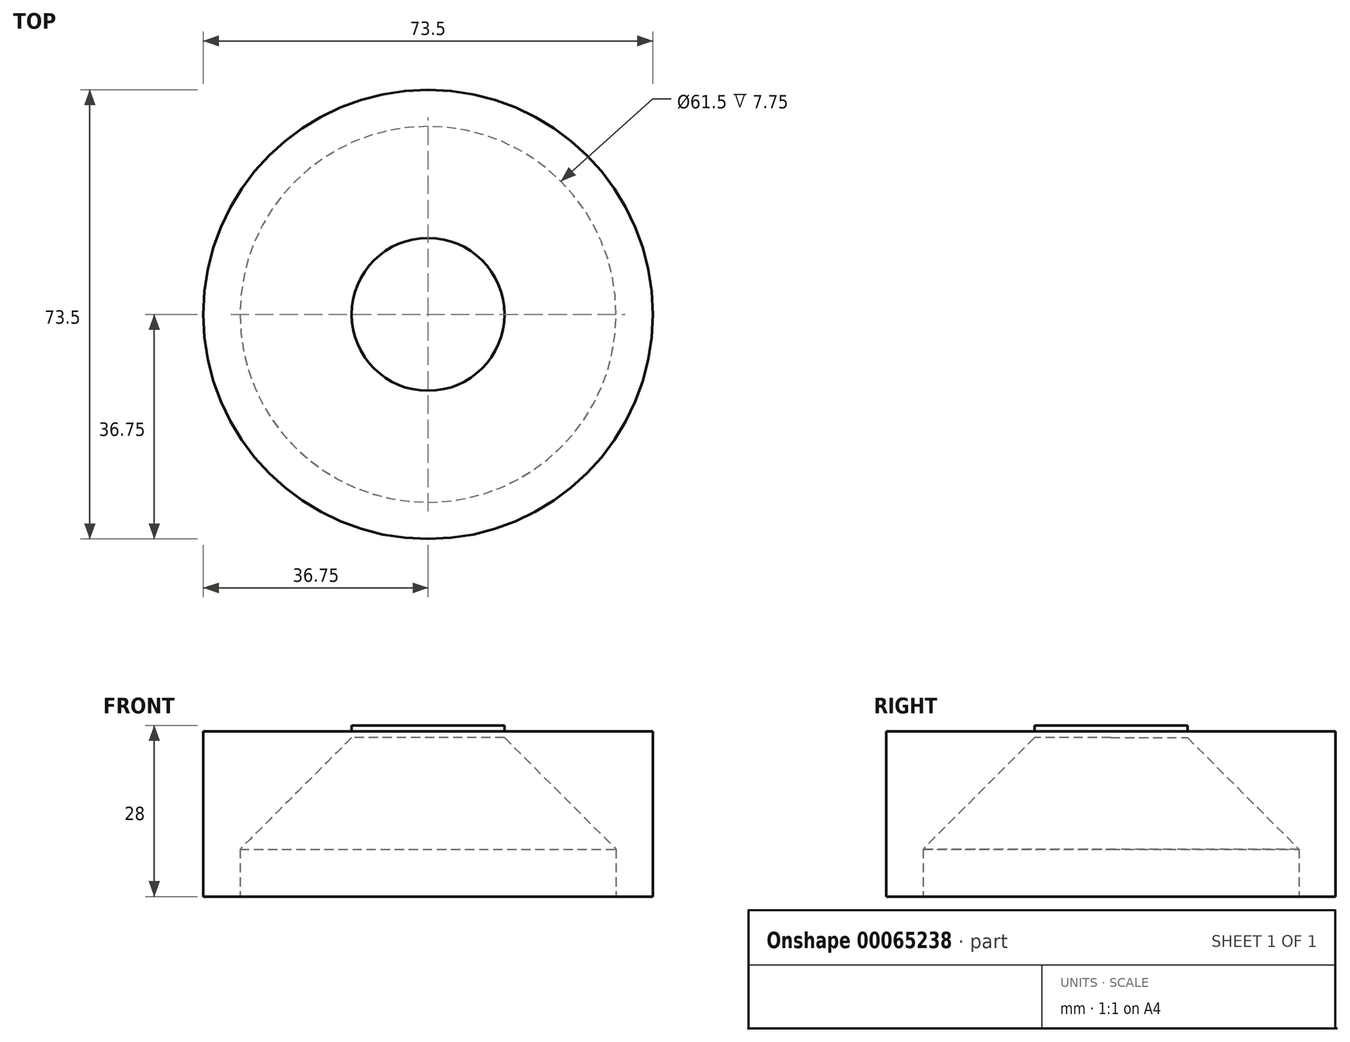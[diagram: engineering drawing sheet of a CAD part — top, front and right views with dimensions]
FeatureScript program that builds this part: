
annotation { "Feature Type Name" : "Feature", "Feature Type Description" : "" }
export const myFeature = defineFeature(function(context is Context, id is Id, definition is map)
    precondition{}
    {
        {
            var Q0;
            Q0=qCreatedBy(makeId("Top.planeOp"),FACE);
            var sketch = newSketch(context, id + "F0", { "sketchPlane" : qUnion([Q0])});
            skCircle(sketch, "E0", {"center": v(0, 0) * mm, "radius": 30.75 * mm});
            skCircle(sketch, "E1.0", {"center": v(0, 0) * mm, "radius": 36.75 * mm});
            skCircle(sketch, "E2", {"center": v(0, 0) * mm, "radius": 12.5 * mm});
            skSolve(sketch);
        }
        {
            var Q0;
            Q0=makeQuery(id+"F0.imprint","IMPRINT",FACE,{"disambiguationData":[TD([[makeQuery(id+"F0.imprint","IMPRINT",EDGE,{"derivedFrom":sQuery(id+"F0.wireOp",EDGE,"E0")}),-1.0]])]});
            var Q1;
            Q1=makeQuery(id+"F0.imprint","IMPRINT",FACE,{"disambiguationData":[TD([[makeQuery(id+"F0.imprint","IMPRINT",EDGE,{"derivedFrom":sQuery(id+"F0.wireOp",EDGE,"E1.0")}),-1.0]])]});
            extrude(context, id + "F1", {"entities" : qUnion([Q0, Q1]), "offsetDistance" : 25 * mm, "depth" : 40 * mm});
        }
        {
            var Q0;
            Q0=makeQuery(id+"F0.imprint","IMPRINT",FACE,{"disambiguationData":[TD([[makeQuery(id+"F0.imprint","IMPRINT",EDGE,{"derivedFrom":sQuery(id+"F0.wireOp",EDGE,"E0")}),1.0]])]});
            extrude(context, id + "F2", {"entities" : qUnion([Q0]), "operationType" : NewBodyOperationType.ADD, "depth" : 40 * mm, "hasSecondDirection" : true, "secondDirectionOppositeDirection" : false, "secondDirectionDepth" : 20 * mm});
        }
        {
            var Q0;
            Q0=makeQuery(id+"F0.imprint","IMPRINT",FACE,{"disambiguationData":[TD([[makeQuery(id+"F0.imprint","IMPRINT",EDGE,{"derivedFrom":sQuery(id+"F0.wireOp",EDGE,"E2")}),1.0]])]});
            extrude(context, id + "F3", {"entities" : qUnion([Q0]), "operationType" : NewBodyOperationType.ADD, "offsetDistance" : 25 * mm, "depth" : 41 * mm, "hasSecondDirection" : true, "secondDirectionOppositeDirection" : false, "secondDirectionDepth" : 39 * mm});
        }
        {
            var Q0;
            Q0=makeQuery(id+"F2.opExtrude","CAP_EDGE",EDGE,{"disambiguationData":[OSD([sQuery(id+"F0.wireOp",EDGE,"E2")])],"isStart":true});
            chamfer(context, id + "F4", {"entities" : qUnion([Q0]), "width" : 19 * mm, "tangentPropagation" : true});
        }
        {
            var Q0;
            Q0=makeQuery(id+"F1.opExtrude","CAP_FACE",FACE,{"disambiguationData":[OSD([sQuery(id+"F0.wireOp",EDGE,"E0"),sQuery(id+"F0.wireOp",EDGE,"E1.0")])],"isStart":true});
            extrude(context, id + "F5", {"entities" : qUnion([Q0]), "operationType" : NewBodyOperationType.REMOVE, "oppositeDirection" : true, "depth" : 13 * mm, "offsetDistance" : 25 * mm});
        }
    });
